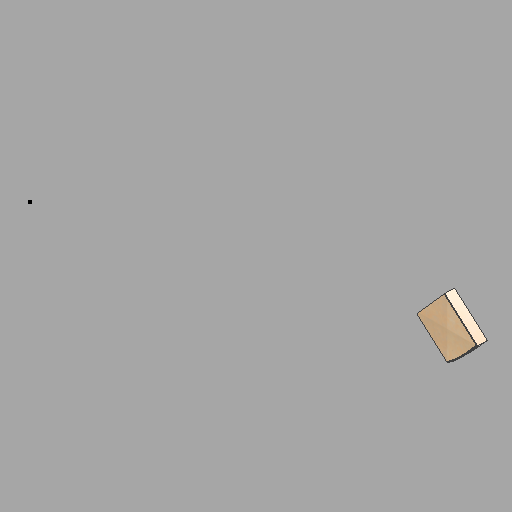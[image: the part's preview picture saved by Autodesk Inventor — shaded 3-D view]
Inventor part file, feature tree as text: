
AUTODESK INVENTOR PART (.ipt)
format: ipt  version: 2022.1 (Build 261234020, 234B)  size: 175,616 bytes
history: native  units: in
note: dims shown in document units (in); Inventor stores cm internally (conversion verified against a paired STEP export)
features: sketch x13, plane x4, other x3
ambient origin geometry x8: Origin, YZ Plane, XZ Plane, XY Plane, X Axis, Y Axis, Z Axis, Center Point
bodies: Solid1 (feature_tree)
feature tree (20):
  other  "Solid18.ipt"
  other  "Solid1::Solid18.ipt"
  other  "TaggingFeature1"
  sketch  "Sketch1"  dims[d0=0.3937in]
  sketch  "Sketch2"
  sketch  "Sketch3"
  sketch  "Sketch4"
  sketch  "Sketch5"
  sketch  "Sketch6"
  sketch  "Sketch12"
  sketch  "Sketch13"
  sketch  "Sketch14"
  sketch  "Sketch15"
  sketch  "Sketch16"
  sketch  "Sketch17"
  sketch  "Sketch19"
  plane  "Work Plane1"
  plane  "Work Plane2"
  plane  "Work Plane5"
  plane  "Work Plane6"
